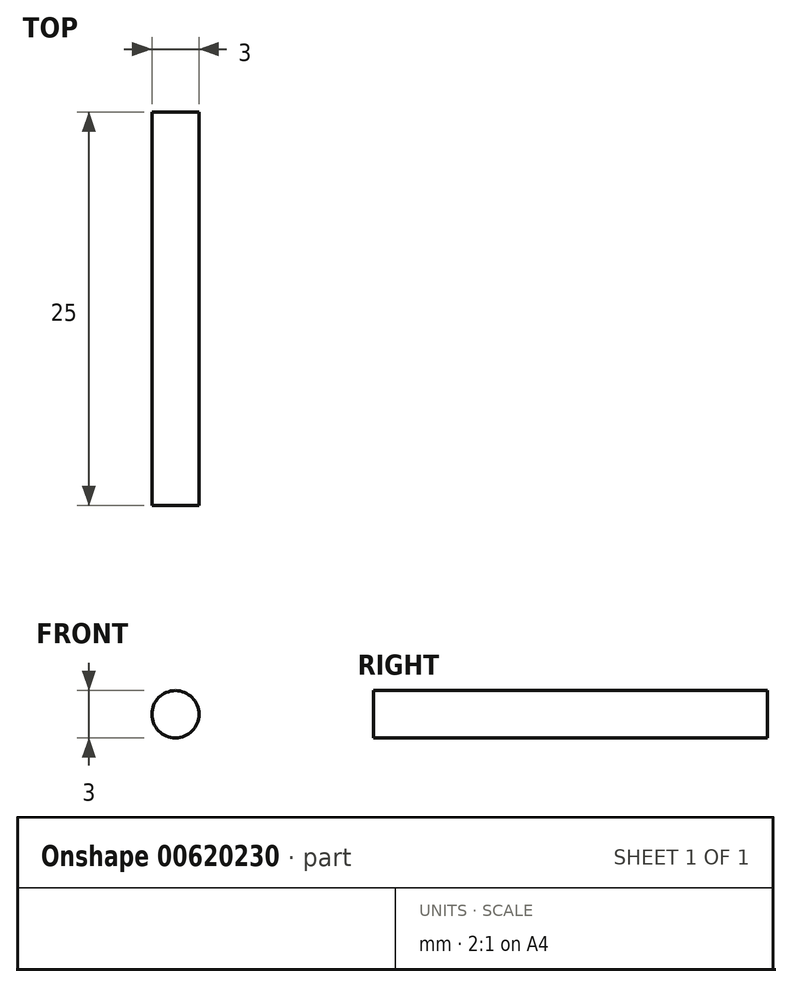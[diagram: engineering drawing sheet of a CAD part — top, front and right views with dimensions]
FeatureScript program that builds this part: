
annotation { "Feature Type Name" : "Feature", "Feature Type Description" : "" }
export const myFeature = defineFeature(function(context is Context, id is Id, definition is map)
    precondition{}
    {
        {
            var Q0;
            Q0=qCreatedBy(makeId("Front.planeOp"),FACE);
            var sketch = newSketch(context, id + "F0", { "sketchPlane" : qUnion([Q0])});
            skCircle(sketch, "E0", {"center": v(0, 0) * mm, "radius": 1.5 * mm});
            skSolve(sketch);
        }
        {
            var Q0;
            Q0 = qSketchRegion(id + "F0", true);
            extrude(context, id + "F1", {"entities" : qUnion([Q0]), "depth" : 25 * mm, "offsetDistance" : 25 * mm});
        }
    });
